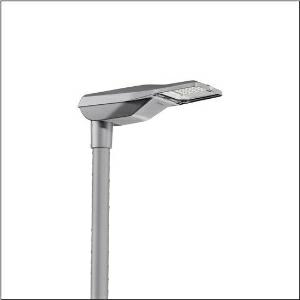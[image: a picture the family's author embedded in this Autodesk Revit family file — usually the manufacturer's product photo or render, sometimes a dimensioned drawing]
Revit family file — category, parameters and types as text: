
# Revit family: streetlight_sl_21_iq_micro___p0_8a_5xe1u31g08cb_6469
name_source: partatom
category: Lighting Fixtures
units: mm (PartAtom-declared; Revit-internal decimal feet)

## family parameters
Cut with Voids When Loaded = No
Host = Face
Light Source = No
Part Type = Normal
Room Calculation Point = No
Round Connector Dimension = Use Diameter
Shared = No

## types (1)
- --- (1 x LED, 2830 lm, 19.4 W, 3000K)
    Apparent Load = 19 VA
    CIE Flux Codes = 33 69 96 100 100
    Color Rendering = 70
    Color Temperature = 3000K
    Default Elevation = 1800 mm
    Description = Streetlight SL 21 iQ micro, mast luminaire, primary light control with lens, of PMMA, primary optical cover: cover, of toughened safety glass, transparent, light distribution: P0.8a, light emission: direct distribution, primary light characteristic: asymmetric, installation type: post-top, side-entry, LED, High Power LED, rated luminous flux: 2.830lm, luminous efficacy: 146lm/W, light colour: 730, colour temperature: 3000K, control gear: iQ Street-Remote, control: pre-setting: linear dimming characteristic, Street-Remote, Auto-Match, Temp-Guard, Lumen-Switch, Night-Set, Smart-Wire, Light-Fading, Desk-Remote (wireless, voltage-free reading and setting of iQ features in the workshop via application-optimized NFC function/RFID function), optimised constant luminous flux control (CLO 2.0), mains connection: 220..240V, AC, 50/60Hz, start of lifetime: 19W, end of service life: 20W, reduction: 10W, luminaire housing, of diecast aluminium, powder-coated, Siteco® metallic grey (DB 702S), corrosivity category C5 mid according to DIN EN ISO 12944, please order mast flange separately, inclination adjustable: 0°, 5°, 10°, 15°, sealing non-destructively replaceable, multi-level sealing system, length: 528mm, width: 235mm, height: 110mm, mast flange for spigot size: 42mm (side-entry): 5XC10008XM4, 60/48mm (side-entry/post-top): 5XC10108XM2, 76/60mm (side-entry/post-top): 5XC10108XM1, protection rating (complete): IP66, insulation class (complete): insulation class II (safety insulation), certification: CE, ENEC, ENEC+, VDE, impact resistance: IK10, permissible operating ambient temperature for outdoor applications: -40..+50°C, standard-compliant lighting for roads and squares, packaging unit: 1 piece

Light Distribution: P0.8a
    Height = 110 mm
    Lamp = 1 x LED
    Lamp Light Flux = 2830 lm
    Lamp Power = 19.4 W
    Lamp count = 1
    Length = 528 mm
    Luminous efficacy = 146 lm/W
    Manufacturer = Siteco
    ModVariant = No
    Model = 5XE1U31G08CB
    Number of Poles = 1
    OnlyDefault = Yes
    Power Factor = 1
    Product Name = Streetlight SL 21 iQ micro | P0.8a
    Product group = mast luminaire | pylon top
    ProductGroupID = 6100
    Protection Class = Protection class II
    Protection Degree = IP 66
    RLX_Detail_Level = 1
    RLX_Emergency_Light_Flux = 0 lm
    RLX_Emergency_Type = 0
    RLX_Emergency_Type_DB = No
    RlxData = <blob elided: 98457 chars, md5=2d321ea7>
    Socket = socket
    Standby Power = 0 W
    System Light Flux = 2830 lm
    System Power = 19 W
    Type Comments = factory setting: luminous flux: 100 % | dim-lin: 254 | 387 mA
    Type Image = l_1006881.jpg
    URL = http://relux.com
    VarID = @adj_073004
    Voltage = 0 V
    Weight = 0.00 kg
    Width = 235 mm

## geometry (parser evidence)
native form markers: Blend x4, Sweep x9
no freeform markers — native parametric forms only
